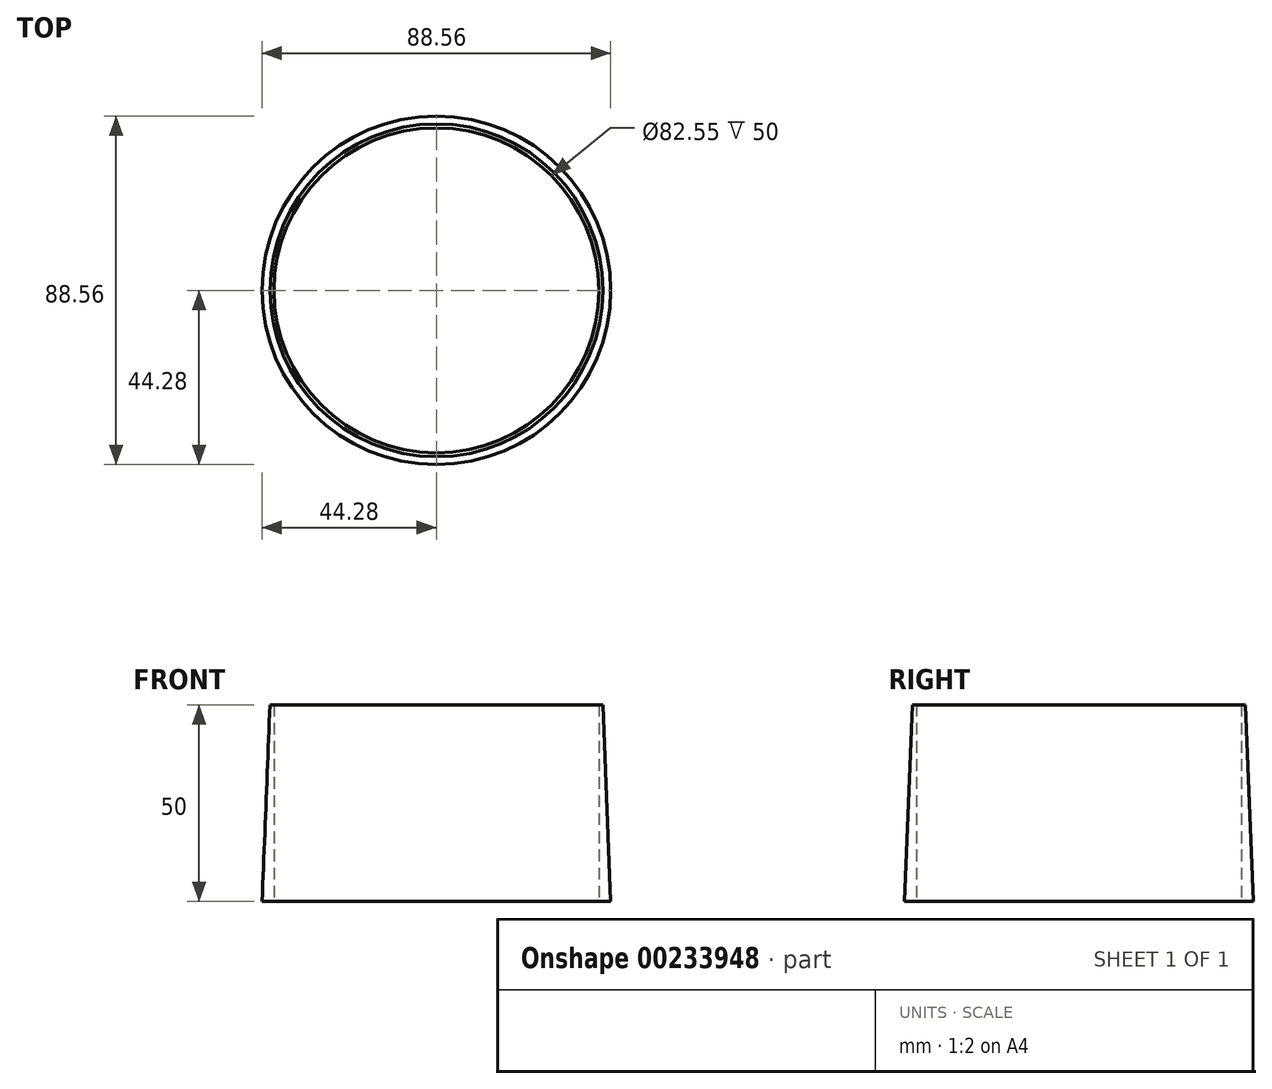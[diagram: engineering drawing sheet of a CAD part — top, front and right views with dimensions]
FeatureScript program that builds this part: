
annotation { "Feature Type Name" : "Feature", "Feature Type Description" : "" }
export const myFeature = defineFeature(function(context is Context, id is Id, definition is map)
    precondition{}
    {
        {
            var Q0;
            Q0=qCreatedBy(makeId("Top.planeOp"),FACE);
            var sketch = newSketch(context, id + "F0", { "sketchPlane" : qUnion([Q0])});
            skCircle(sketch, "E0", {"center": v(0, 0) * mm, "radius": 41.27 * mm});
            skCircle(sketch, "E1", {"center": v(0, 0) * mm, "radius": 42.27 * mm});
            skSolve(sketch);
        }
        {
            var Q0;
            Q0 = qSketchRegion(id + "F0", true);
            extrude(context, id + "F1", {"entities" : qUnion([Q0]), "depth" : 50 * mm});
        }
        {
            var Q0;
            Q0=qCreatedBy(makeId("Front.planeOp"),FACE);
            var sketch = newSketch(context, id + "F2", { "sketchPlane" : qUnion([Q0])});
            skLineSegment(sketch, "E2", {"start": v(-44.27, 0) * mm, "end": v(-42.27, 50) * mm});
            skLineSegment(sketch, "E3", {"start": v(-42.27, 50) * mm, "end": v(-42.27, 0) * mm});
            skLineSegment(sketch, "E4", {"start": v(-42.27, 0) * mm, "end": v(-44.27, 0) * mm});
            skLineSegment(sketch, "E5", {"start": v(-42.27, 0) * mm, "end": v(-42.27, 50) * mm});
            skSolve(sketch);
        }
        {
            var Q0;
            Q0=qCreatedBy(makeId("Front.planeOp"),FACE);
            var sketch = newSketch(context, id + "F3", { "sketchPlane" : qUnion([Q0])});
            skLineSegment(sketch, "E6", {"start": v(0, 0) * mm, "end": v(0, 64.39) * mm});
            skSolve(sketch);
        }
        {
            var Q0;
            Q0 = qSketchRegion(id + "F2", true);
            var Q1;
            Q1=sQuery(id+"F3.wireOp",EDGE,"E6");
            revolve(context, id + "F4", {"operationType" : NewBodyOperationType.ADD, "entities" : qUnion([Q0]), "axis" : qUnion([Q1]), "revolveType" : RevolveType.FULL});
        }
    });
